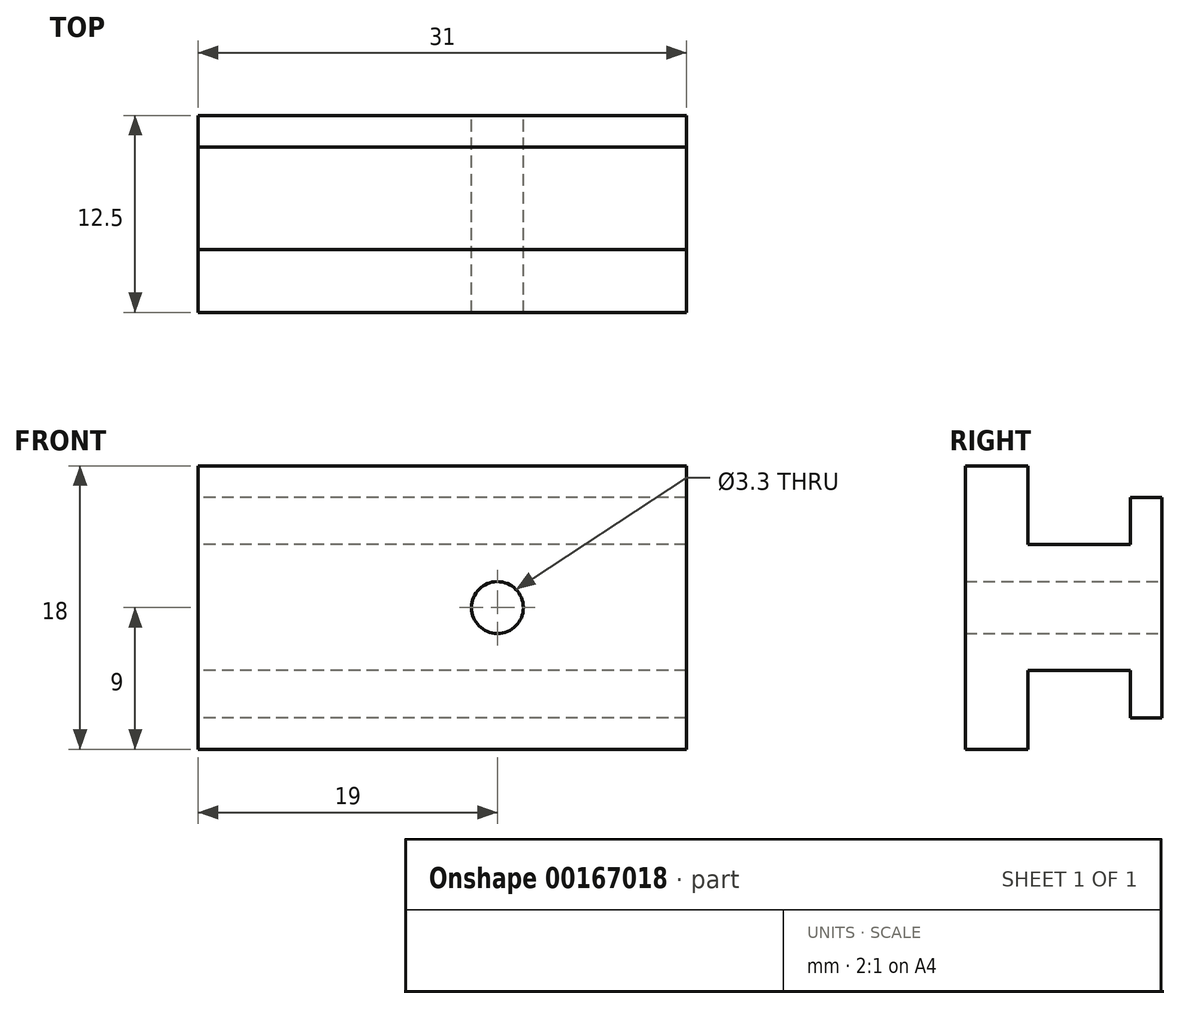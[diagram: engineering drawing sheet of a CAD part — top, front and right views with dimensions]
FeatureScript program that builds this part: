
annotation { "Feature Type Name" : "Feature", "Feature Type Description" : "" }
export const myFeature = defineFeature(function(context is Context, id is Id, definition is map)
    precondition{}
    {
        {
            var Q0;
            Q0=qCreatedBy(makeId("Right.planeOp"),FACE);
            var sketch = newSketch(context, id + "F0", { "sketchPlane" : qUnion([Q0])});
            skLineSegment(sketch, "E0", {"start": v(0, 15) * mm, "end": v(6.1, 15) * mm});
            skLineSegment(sketch, "E1", {"start": v(20, 20) * mm, "end": v(15, 20) * mm});
            skLineSegment(sketch, "E2.0", {"start": v(15, 20) * mm, "end": v(15, 24) * mm});
            skLineSegment(sketch, "E3.0", {"start": v(11, 24) * mm, "end": v(11, 15) * mm});
            skLineSegment(sketch, "E4.trimOffspring", {"start": v(15, 24) * mm, "end": v(11, 24) * mm});
            skLineSegment(sketch, "E5", {"start": v(15, 20) * mm, "end": v(15, 19) * mm});
            skLineSegment(sketch, "E6", {"start": v(15, 19) * mm, "end": v(21.5, 19) * mm});
            skLineSegment(sketch, "E7", {"start": v(21.5, 19) * mm, "end": v(21.5, 22) * mm});
            skLineSegment(sketch, "E8", {"start": v(21.5, 22) * mm, "end": v(23.5, 22) * mm});
            skLineSegment(sketch, "E9", {"start": v(23.5, 22) * mm, "end": v(23.5, 15) * mm});
            skLineSegment(sketch, "E10.MirrorCS", {"start": v(15, 10) * mm, "end": v(15, 11) * mm});
            skLineSegment(sketch, "E11.MirrorCS", {"start": v(20, 10) * mm, "end": v(15, 10) * mm});
            skLineSegment(sketch, "E12.MirrorCS", {"start": v(21.5, 8) * mm, "end": v(23.5, 8) * mm});
            skLineSegment(sketch, "E13.MirrorCS", {"start": v(23.5, 8) * mm, "end": v(23.5, 15) * mm});
            skLineSegment(sketch, "E14.MirrorCS", {"start": v(21.5, 11) * mm, "end": v(21.5, 8) * mm});
            skLineSegment(sketch, "E15.MirrorCS", {"start": v(15, 11) * mm, "end": v(21.5, 11) * mm});
            skLineSegment(sketch, "E16.MirrorCS", {"start": v(15, 6) * mm, "end": v(11, 6) * mm});
            skLineSegment(sketch, "E17.MirrorCS", {"start": v(11, 6) * mm, "end": v(11, 15) * mm});
            skLineSegment(sketch, "E18.MirrorCS", {"start": v(15, 10) * mm, "end": v(15, 6) * mm});
            skSolve(sketch);
        }
        {
            var Q0;
            Q0=qSketchRegion(id+"F0",true);
            extrude(context, id + "F1", {"entities" : qUnion([Q0]), "depth" : 38 * mm});
        }
        {
            var Q0;
            Q0=makeQuery(id+"F1.opExtrude","SWEPT_FACE",FACE,{"disambiguationData":[OSD([sQuery(id+"F0.wireOp",EDGE,"E9"),sQuery(id+"F0.wireOp",EDGE,"3e864bbd-24f3-4d39-9146-677a4ecd5e8a0.MirrorCS")])]});
            var sketch = newSketch(context, id + "F2", { "sketchPlane" : qUnion([Q0])});
            skLineSegment(sketch, "E19", {"start": v(-19, 22) * mm, "end": v(-19, 8) * mm});
            skCircle(sketch, "E20", {"center": v(-19, 15) * mm, "radius": 1.65 * mm});
            skSolve(sketch);
        }
        {
            var Q0;
            Q0=qSketchRegion(id+"F2",true);
            extrude(context, id + "F3", {"entities" : qUnion([Q0]), "operationType" : NewBodyOperationType.REMOVE, "oppositeDirection" : true, "depth" : 25 * mm});
        }
        {
            var Q0;
            Q0=makeQuery(id+"F1.opExtrude","CAP_FACE",FACE,{"disambiguationData":[OSD([sQuery(id+"F0.wireOp",EDGE,"E2.0"),sQuery(id+"F0.wireOp",EDGE,"E3.0"),sQuery(id+"F0.wireOp",EDGE,"E4.trimOffspring"),sQuery(id+"F0.wireOp",EDGE,"E5"),sQuery(id+"F0.wireOp",EDGE,"E6"),sQuery(id+"F0.wireOp",EDGE,"E7"),sQuery(id+"F0.wireOp",EDGE,"E8"),sQuery(id+"F0.wireOp",EDGE,"E9"),sQuery(id+"F0.wireOp",EDGE,"E10.MirrorCS"),sQuery(id+"F0.wireOp",EDGE,"E12.MirrorCS"),sQuery(id+"F0.wireOp",EDGE,"E13.MirrorCS"),sQuery(id+"F0.wireOp",EDGE,"E14.MirrorCS"),sQuery(id+"F0.wireOp",EDGE,"E15.MirrorCS"),sQuery(id+"F0.wireOp",EDGE,"E16.MirrorCS"),sQuery(id+"F0.wireOp",EDGE,"E17.MirrorCS"),sQuery(id+"F0.wireOp",EDGE,"E18.MirrorCS")])],"isStart":false});
            extrude(context, id + "F4", {"entities" : qUnion([Q0]), "operationType" : NewBodyOperationType.REMOVE, "oppositeDirection" : true, "depth" : 7 * mm, "offsetDistance" : 25 * mm});
        }
    });
